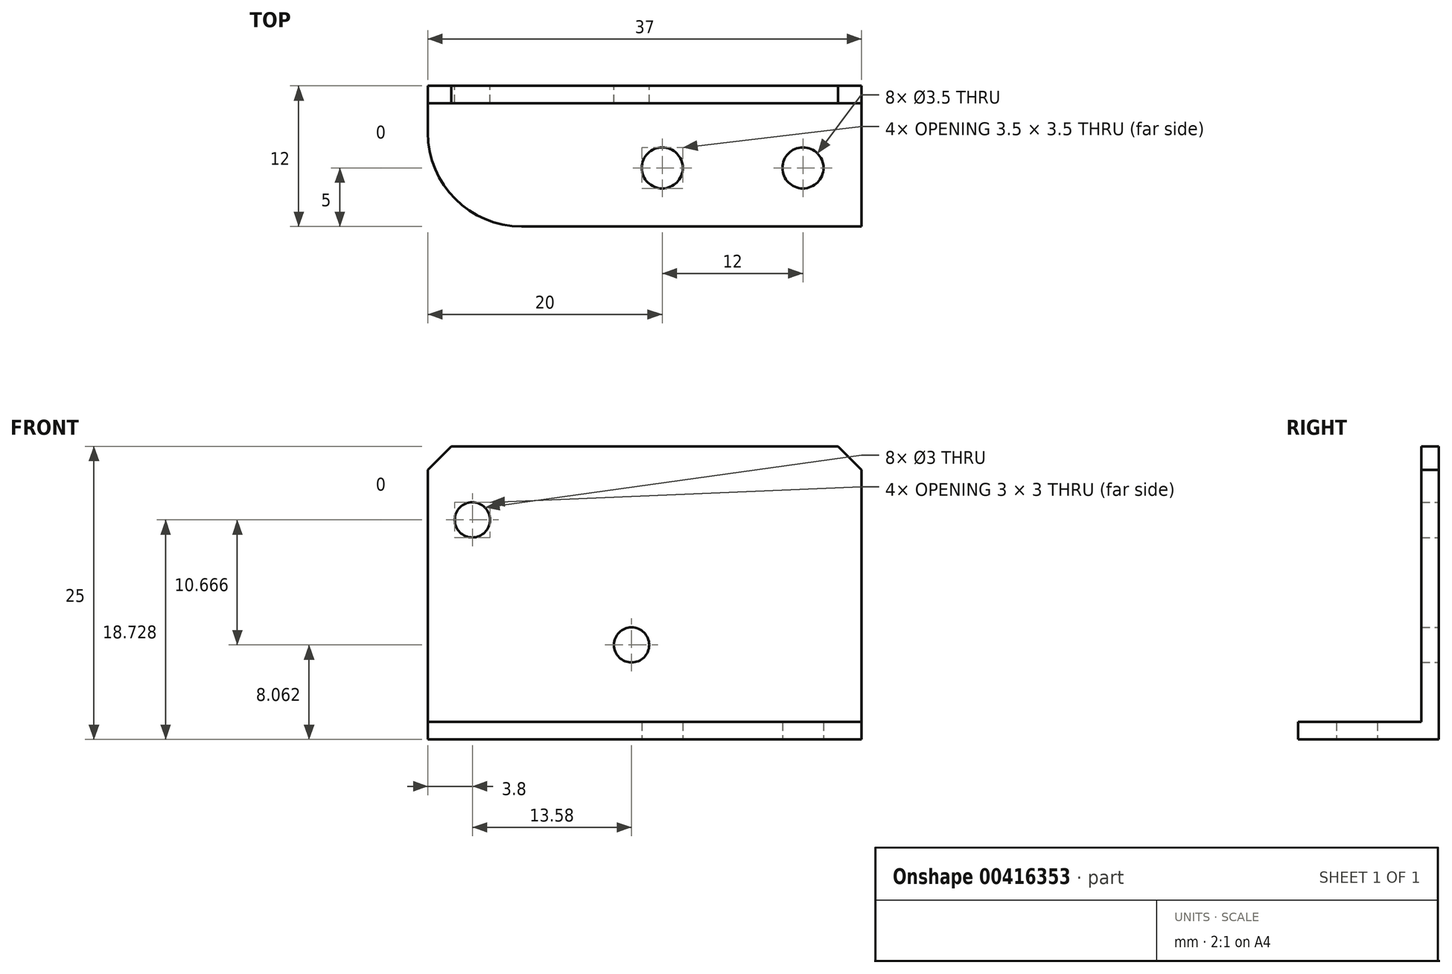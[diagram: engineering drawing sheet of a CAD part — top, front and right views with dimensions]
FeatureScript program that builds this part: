
annotation { "Feature Type Name" : "Feature", "Feature Type Description" : "" }
export const myFeature = defineFeature(function(context is Context, id is Id, definition is map)
    precondition{}
    {
        {
            var Q0;
            Q0=qCreatedBy(makeId("Right.planeOp"),FACE);
            var sketch = newSketch(context, id + "F0", { "sketchPlane" : qUnion([Q0])});
            skLineSegment(sketch, "E0", {"start": v(0, 0) * mm, "end": v(-12, 0) * mm});
            skLineSegment(sketch, "E1", {"start": v(-12, 0) * mm, "end": v(0, 0) * mm});
            skLineSegment(sketch, "E2", {"start": v(0, 0) * mm, "end": v(0, 25) * mm});
            skLineSegment(sketch, "E3.0", {"start": v(-1.5, 1.5) * mm, "end": v(-1.5, 25) * mm});
            skLineSegment(sketch, "E3.1", {"start": v(-12, 1.5) * mm, "end": v(-1.5, 1.5) * mm});
            skLineSegment(sketch, "E4", {"start": v(-1.5, 25) * mm, "end": v(0, 25) * mm});
            skLineSegment(sketch, "E5", {"start": v(-12, 0) * mm, "end": v(-12, 1.5) * mm});
            skSolve(sketch);
        }
        {
            var Q0;
            Q0 = qSketchRegion(id + "F0", true);
            extrude(context, id + "F1", {"entities" : qUnion([Q0]), "oppositeDirection" : true, "depth" : 37 * mm});
        }
        {
            var Q0;
            Q0=qCreatedBy(makeId("Front.planeOp"),FACE);
            var sketch = newSketch(context, id + "F2", { "sketchPlane" : qUnion([Q0])});
            skCircle(sketch, "E6", {"center": v(-33.2, 18.73) * mm, "radius": 1.5 * mm});
            skCircle(sketch, "E7", {"center": v(-19.62, 8.06) * mm, "radius": 1.5 * mm});
            skSolve(sketch);
        }
        {
            var Q0;
            Q0 = qSketchRegion(id + "F2", true);
            extrude(context, id + "F3", {"entities" : qUnion([Q0]), "operationType" : NewBodyOperationType.REMOVE, "endBound" : BoundingType.THROUGH_ALL, "depth" : 25 * mm});
        }
        {
            var Q0;
            Q0=qCreatedBy(makeId("Top.planeOp"),FACE);
            var sketch = newSketch(context, id + "F4", { "sketchPlane" : qUnion([Q0])});
            skCircle(sketch, "E8", {"center": v(-5, -7) * mm, "radius": 1.75 * mm});
            skCircle(sketch, "E9", {"center": v(-17, -7) * mm, "radius": 1.75 * mm});
            skLineSegment(sketch, "E10", {"start": v(-17, -7) * mm, "end": v(-5, -7) * mm, "construction": true});
            skSolve(sketch);
        }
        {
            var Q0;
            Q0 = qSketchRegion(id + "F4", true);
            extrude(context, id + "F5", {"entities" : qUnion([Q0]), "operationType" : NewBodyOperationType.REMOVE, "endBound" : BoundingType.THROUGH_ALL, "depth" : 25 * mm});
        }
        {
            var Q0;
            Q0=makeQuery(id+"F1.opExtrude","CAP_EDGE",EDGE,{"disambiguationData":[OSD([sQuery(id+"F0.wireOp",EDGE,"E5")])],"isStart":false});
            fillet(context, id + "F6", {"entities" : qUnion([Q0]), "radius" : 8 * mm, "tangentPropagation" : true, "allowEdgeOverflow" : false});
        }
        {
            var Q0;
            Q0=makeQuery(id+"F1.opExtrude","CAP_EDGE",EDGE,{"disambiguationData":[OSD([sQuery(id+"F0.wireOp",EDGE,"E4")])],"isStart":false});
            var Q1;
            Q1=makeQuery(id+"F1.opExtrude","CAP_EDGE",EDGE,{"disambiguationData":[OSD([sQuery(id+"F0.wireOp",EDGE,"E4")])],"isStart":true});
            chamfer(context, id + "F7", {"entities" : qUnion([Q0, Q1]), "width" : 2 * mm, "tangentPropagation" : true});
        }
    });
